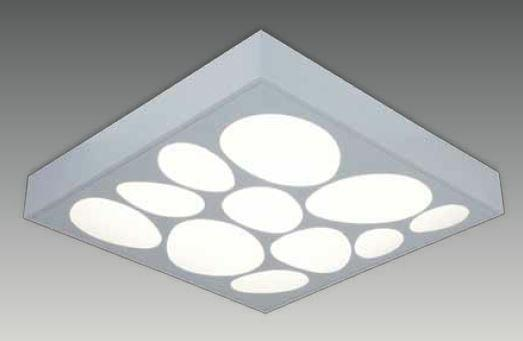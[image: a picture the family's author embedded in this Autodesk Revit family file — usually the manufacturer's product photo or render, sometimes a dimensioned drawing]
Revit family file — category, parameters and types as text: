
# Revit family: SD 6060 BIO
name_source: partatom
category: Lighting Fixtures
revit_build: Autodesk Revit 2017 (Build: 20160225_1515(x64)
units: mm (PartAtom-declared; Revit-internal decimal feet)

## family parameters
Cut with Voids When Loaded = No
Host = Face
Light Source = Yes
Part Type = Normal
Room Calculation Point = No
Round Connector Dimension = Use Diameter
Shared = No

## types (4) — shared parameters
Color Filter = 16777215
Default Elevation = 1219 mm
Dimming Lamp Color Temperature Shift = <None>
Emit Shape Visible in Rendering = Yes
Emit from Rectangle Length = 570 mm  [stored 1.87008 ft]
Emit from Rectangle Width = 570 mm  [stored 1.87008 ft]
Light Source Symbol Size = 610 mm
Manufacturer = ARLIGHT
Type Image = SD 6060 BIO.JPG

## per-type parameters (varying)
| type | Wattage Comments |
| SDBIO.6060.36.30 | 36 |
| SDBIO.6060.36.40 | 36 |
| SDBIO.6060.28.30 | 28 |
| SDBIO.6060.28.40 | 28 |

note: [stored X ft] marks values corroborated as IEEE doubles in the binary element streams (Revit-internal decimal feet)

## geometry (parser evidence)
native form markers: Sweep x3
no freeform markers — native parametric forms only
